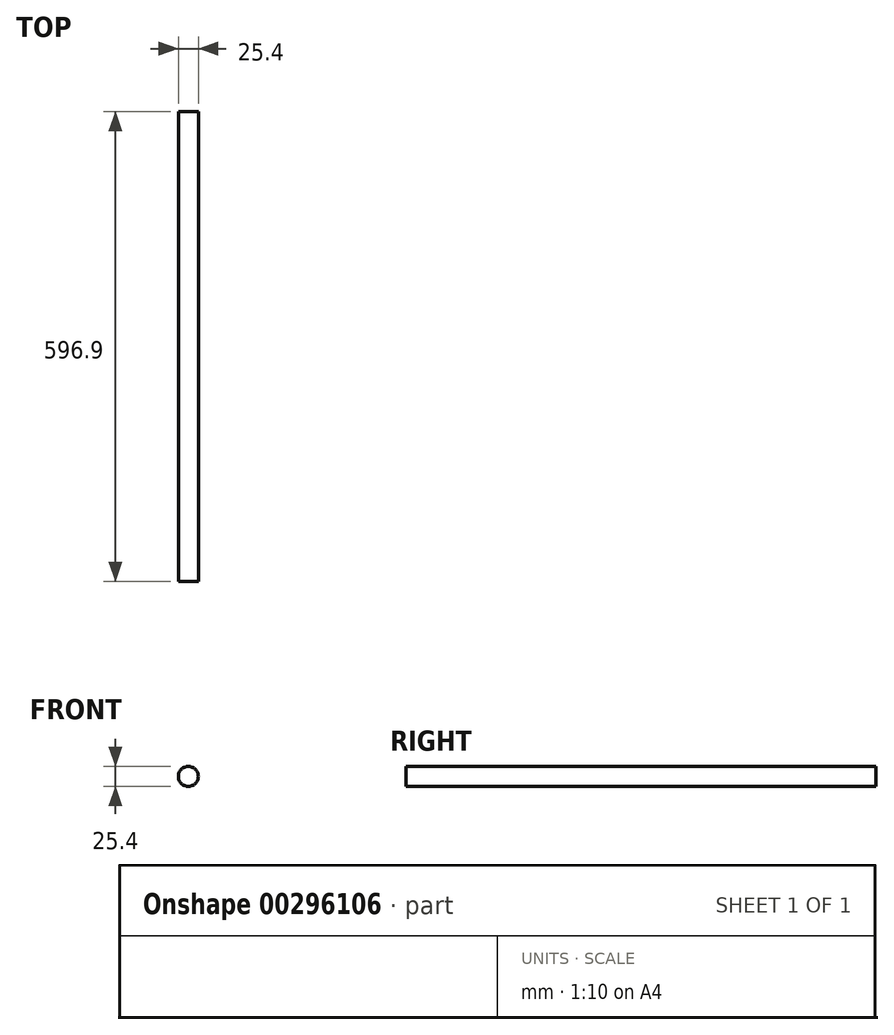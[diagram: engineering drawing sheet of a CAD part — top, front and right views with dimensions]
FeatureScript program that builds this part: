
annotation { "Feature Type Name" : "Feature", "Feature Type Description" : "" }
export const myFeature = defineFeature(function(context is Context, id is Id, definition is map)
    precondition{}
    {
        {
            var Q0;
            Q0=qCreatedBy(makeId("Front.planeOp"),FACE);
            var sketch = newSketch(context, id + "F0", { "sketchPlane" : qUnion([Q0])});
            skCircle(sketch, "E0", {"center": v(0, 0) * mm, "radius": 12.7 * mm});
            skSolve(sketch);
        }
        {
            var Q0;
            Q0=makeQuery(id+"F0.imprint","IMPRINT",FACE,{"disambiguationData":[TD([[makeQuery(id+"F0.imprint","IMPRINT",EDGE,{"derivedFrom":sQuery(id+"F0.wireOp",EDGE,"E0")}),1.0]])]});
            extrude(context, id + "F1", {"entities" : qUnion([Q0]), "depth" : 596.9 * mm});
        }
    });
